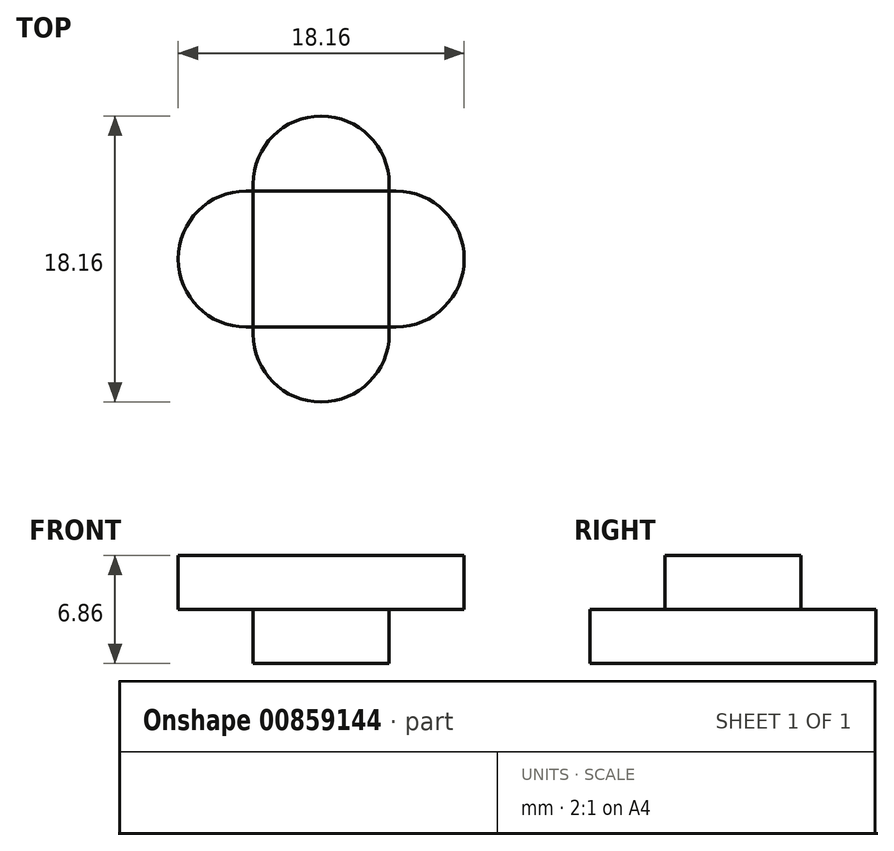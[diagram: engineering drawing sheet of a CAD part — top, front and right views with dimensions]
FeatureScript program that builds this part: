
annotation { "Feature Type Name" : "Feature", "Feature Type Description" : "" }
export const myFeature = defineFeature(function(context is Context, id is Id, definition is map)
    precondition{}
    {
        {
            var Q0;
            Q0=qCreatedBy(makeId("Top.planeOp"),FACE);
            var sketch = newSketch(context, id + "F0", { "sketchPlane" : qUnion([Q0])});
            skLineSegment(sketch, "E0.bottom", {"start": v(4.76, -4.32) * mm, "end": v(-4.76, -4.32) * mm});
            skLineSegment(sketch, "E0.top", {"start": v(4.76, 4.32) * mm, "end": v(-4.76, 4.32) * mm});
            skLineSegment(sketch, "E0.left", {"start": v(4.76, -4.32) * mm, "end": v(4.76, 4.32) * mm, "construction": true});
            skLineSegment(sketch, "E0.right", {"start": v(-4.76, -4.32) * mm, "end": v(-4.76, 4.32) * mm, "construction": true});
            skPoint(sketch, "E0.middle", {"position": v(0, 0) * mm});
            skArc(sketch, "E1", {"start": v(4.76, -4.32) * mm, "mid": v(9.08, 0) * mm, "end": v(4.76, 4.32) * mm});
            skArc(sketch, "E2", {"start": v(-4.76, 4.32) * mm, "mid": v(-9.08, 0) * mm, "end": v(-4.76, -4.32) * mm});
            skCircle(sketch, "E3", {"center": v(0, 0) * mm, "radius": 4.32 * mm, "construction": true});
            skLineSegment(sketch, "E4.bottom", {"start": v(4.32, -4.76) * mm, "end": v(-4.32, -4.76) * mm, "construction": true});
            skLineSegment(sketch, "E4.top", {"start": v(4.32, 4.76) * mm, "end": v(-4.32, 4.76) * mm, "construction": true});
            skLineSegment(sketch, "E4.left", {"start": v(4.32, -4.76) * mm, "end": v(4.32, 4.76) * mm});
            skLineSegment(sketch, "E4.right", {"start": v(-4.32, -4.76) * mm, "end": v(-4.32, 4.76) * mm});
            skArc(sketch, "E5", {"start": v(-4.32, -4.76) * mm, "mid": v(0, -9.08) * mm, "end": v(4.32, -4.76) * mm});
            skArc(sketch, "E6", {"start": v(4.32, 4.76) * mm, "mid": v(0, 9.08) * mm, "end": v(-4.32, 4.76) * mm});
            skSolve(sketch);
        }
        {
            var Q0;
            Q0=sQuery(id+"F0.wireOp",EDGE,"E0.top");
            var Q1;
            Q1=sQuery(id+"F0.wireOp",EDGE,"E0.bottom");
            var Q2;
            Q2=sQuery(id+"F0.wireOp",EDGE,"E1");
            var Q3;
            Q3=sQuery(id+"F0.wireOp",EDGE,"E2");
            extrude(context, id + "F1", {"bodyType" : ToolBodyType.SURFACE, "surfaceEntities" : qUnion([Q0, Q1, Q2, Q3]), "depth" : 3.43 * mm, "offsetDistance" : 25.4 * mm});
        }
        {
            var Q0;
            Q0=sQuery(id+"F0.wireOp",EDGE,"E5");
            var Q1;
            Q1=sQuery(id+"F0.wireOp",EDGE,"E4.right");
            var Q2;
            Q2=sQuery(id+"F0.wireOp",EDGE,"E6");
            var Q3;
            Q3=sQuery(id+"F0.wireOp",EDGE,"E4.left");
            extrude(context, id + "F2", {"bodyType" : ToolBodyType.SURFACE, "surfaceEntities" : qUnion([Q0, Q1, Q2, Q3]), "oppositeDirection" : true, "depth" : 3.43 * mm, "offsetDistance" : 25.4 * mm});
        }
    });
